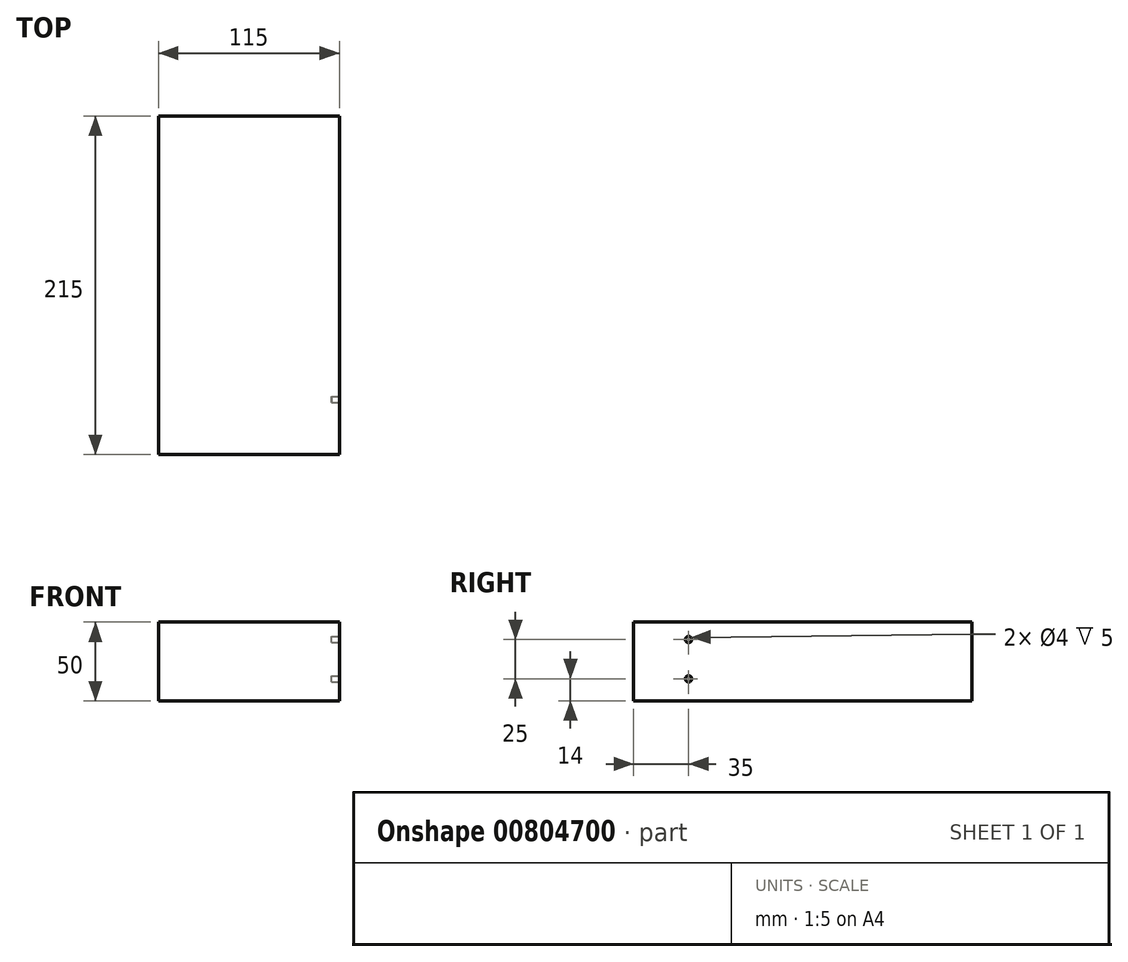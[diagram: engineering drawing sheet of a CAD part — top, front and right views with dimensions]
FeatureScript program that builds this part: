
annotation { "Feature Type Name" : "Feature", "Feature Type Description" : "" }
export const myFeature = defineFeature(function(context is Context, id is Id, definition is map)
    precondition{}
    {
        {
            var Q0;
            Q0=qCreatedBy(makeId("Top.planeOp"),FACE);
            var sketch = newSketch(context, id + "F0", { "sketchPlane" : qUnion([Q0])});
            skLineSegment(sketch, "E0.bottom", {"start": v(57.5, -107.5) * mm, "end": v(-57.5, -107.5) * mm});
            skLineSegment(sketch, "E0.top", {"start": v(57.5, 107.5) * mm, "end": v(-57.5, 107.5) * mm});
            skLineSegment(sketch, "E0.left", {"start": v(57.5, -107.5) * mm, "end": v(57.5, 107.5) * mm});
            skLineSegment(sketch, "E0.right", {"start": v(-57.5, -107.5) * mm, "end": v(-57.5, 107.5) * mm});
            skPoint(sketch, "E0.middle", {"position": v(0, 0) * mm});
            skSolve(sketch);
        }
        {
            var Q0;
            Q0=qSketchRegion(id+"F0",true);
            extrude(context, id + "F1", {"entities" : qUnion([Q0]), "depth" : 50 * mm, "offsetDistance" : 25 * mm});
        }
        {
            var Q0;
            Q0=makeQuery(id+"F1.opExtrude","SWEPT_FACE",FACE,{"disambiguationData":[OSD([sQuery(id+"F0.wireOp",EDGE,"E0.left")])]});
            var sketch = newSketch(context, id + "F2", { "sketchPlane" : qUnion([Q0])});
            skCircle(sketch, "E1", {"center": v(-72.5, 39) * mm, "radius": 2 * mm});
            skCircle(sketch, "E2", {"center": v(-72.5, 14) * mm, "radius": 2 * mm});
            skSolve(sketch);
        }
        {
            var Q0;
            Q0=makeQuery(id+"F2.imprint","IMPRINT",FACE,{"disambiguationData":[TD([[makeQuery(id+"F2.imprint","IMPRINT",EDGE,{"derivedFrom":sQuery(id+"F2.wireOp",EDGE,"E1")}),1.0]])]});
            var Q1;
            Q1=makeQuery(id+"F2.imprint","IMPRINT",FACE,{"disambiguationData":[TD([[makeQuery(id+"F2.imprint","IMPRINT",EDGE,{"derivedFrom":sQuery(id+"F2.wireOp",EDGE,"E2")}),1.0]])]});
            extrude(context, id + "F3", {"entities" : qUnion([Q0, Q1]), "operationType" : NewBodyOperationType.REMOVE, "oppositeDirection" : true, "depth" : 5 * mm, "offsetDistance" : 25 * mm});
        }
    });
